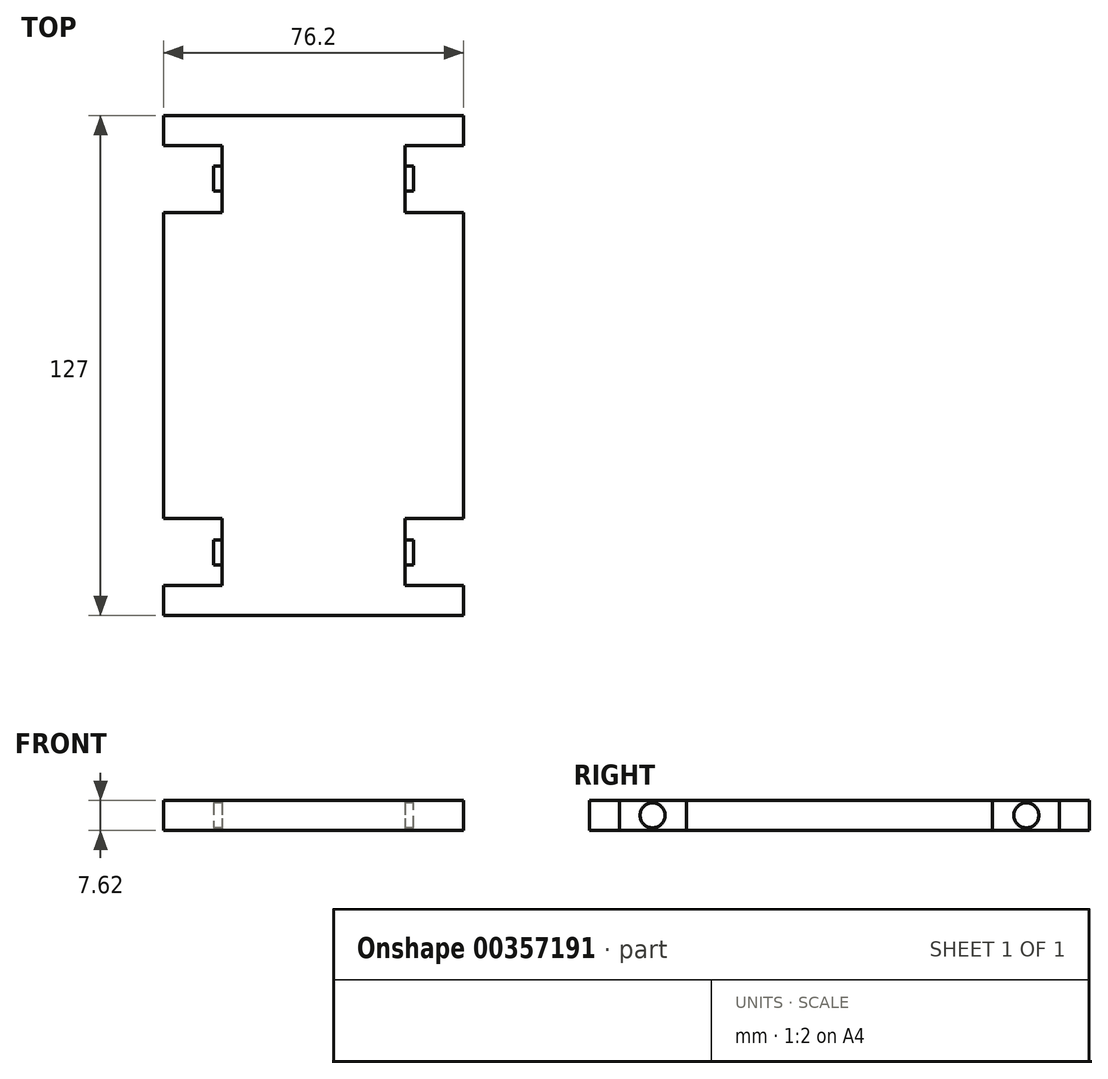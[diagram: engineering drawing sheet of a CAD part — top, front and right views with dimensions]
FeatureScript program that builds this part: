
annotation { "Feature Type Name" : "Feature", "Feature Type Description" : "" }
export const myFeature = defineFeature(function(context is Context, id is Id, definition is map)
    precondition{}
    {
        {
            var Q0;
            Q0=qCreatedBy(makeId("Top.planeOp"),FACE);
            var sketch = newSketch(context, id + "F0", { "sketchPlane" : qUnion([Q0])});
            skLineSegment(sketch, "E0.bottom", {"start": v(30.48, 63.5) * mm, "end": v(-30.48, 63.5) * mm});
            skLineSegment(sketch, "E0.top", {"start": v(38.1, -63.5) * mm, "end": v(-38.1, -63.5) * mm});
            skLineSegment(sketch, "E0.left", {"start": v(38.1, 38.82) * mm, "end": v(38.1, -38.82) * mm});
            skLineSegment(sketch, "E0.right", {"start": v(-38.1, 38.82) * mm, "end": v(-38.1, -38.82) * mm});
            skPoint(sketch, "E0.middle", {"position": v(0, 0) * mm});
            skPoint(sketch, "E1.visualSharp", {"position": v(-38.1, 63.5) * mm});
            skPoint(sketch, "E2.visualSharp", {"position": v(38.1, 63.5) * mm});
            skLineSegment(sketch, "E3", {"start": v(-38.1, 55.88) * mm, "end": v(-23.25, 55.88) * mm});
            skLineSegment(sketch, "E4", {"start": v(-23.25, 55.88) * mm, "end": v(-23.25, 38.82) * mm});
            skLineSegment(sketch, "E5", {"start": v(-23.25, 38.82) * mm, "end": v(-38.1, 38.82) * mm});
            skLineSegment(sketch, "E6.MirrorCS", {"start": v(38.1, 55.88) * mm, "end": v(23.25, 55.88) * mm});
            skLineSegment(sketch, "E7.MirrorCS", {"start": v(23.25, 55.88) * mm, "end": v(23.25, 38.82) * mm});
            skLineSegment(sketch, "E8.MirrorCS", {"start": v(23.25, 38.82) * mm, "end": v(38.1, 38.82) * mm});
            skLineSegment(sketch, "E9.MirrorCS", {"start": v(-23.25, -38.82) * mm, "end": v(-38.1, -38.82) * mm});
            skLineSegment(sketch, "E10.MirrorCS", {"start": v(-23.25, -55.88) * mm, "end": v(-23.25, -38.82) * mm});
            skLineSegment(sketch, "E11.MirrorCS", {"start": v(-38.1, -55.88) * mm, "end": v(-23.25, -55.88) * mm});
            skLineSegment(sketch, "E12.MirrorCS", {"start": v(23.25, -55.88) * mm, "end": v(23.25, -38.82) * mm});
            skLineSegment(sketch, "E13.MirrorCS", {"start": v(38.1, -55.88) * mm, "end": v(23.25, -55.88) * mm});
            skLineSegment(sketch, "E14.MirrorCS", {"start": v(23.25, -38.82) * mm, "end": v(38.1, -38.82) * mm});
            skLineSegment(sketch, "E15.trimOffspring", {"start": v(38.1, -55.88) * mm, "end": v(38.1, -63.5) * mm});
            skLineSegment(sketch, "E16.trimOffspring", {"start": v(-38.1, -55.88) * mm, "end": v(-38.1, -63.5) * mm});
            skLineSegment(sketch, "E17", {"start": v(-30.48, 63.5) * mm, "end": v(-38.1, 63.5) * mm});
            skLineSegment(sketch, "E18", {"start": v(-38.1, 63.5) * mm, "end": v(-38.1, 55.88) * mm});
            skLineSegment(sketch, "E19", {"start": v(30.48, 63.5) * mm, "end": v(38.1, 63.5) * mm});
            skLineSegment(sketch, "E20", {"start": v(38.1, 63.5) * mm, "end": v(38.1, 55.88) * mm});
            skSolve(sketch);
        }
        {
            var Q0;
            Q0 = qSketchRegion(id + "F0", true);
            extrude(context, id + "F1", {"entities" : qUnion([Q0]), "endBound" : BoundingType.SYMMETRIC, "depth" : 7.62 * mm});
        }
        {
            var Q0;
            Q0=qCreatedBy(makeId("Right.planeOp"),FACE);
            var sketch = newSketch(context, id + "F2", { "sketchPlane" : qUnion([Q0])});
            skCircle(sketch, "E21", {"center": v(-47.5, 0) * mm, "radius": 3.18 * mm});
            skCircle(sketch, "E22.MirrorC", {"center": v(47.5, 0) * mm, "radius": 3.18 * mm});
            skSolve(sketch);
        }
        {
            var Q0;
            Q0 = qSketchRegion(id + "F2", true);
            extrude(context, id + "F3", {"entities" : qUnion([Q0]), "operationType" : NewBodyOperationType.ADD, "endBound" : BoundingType.SYMMETRIC, "depth" : 50.8 * mm});
        }
    });
